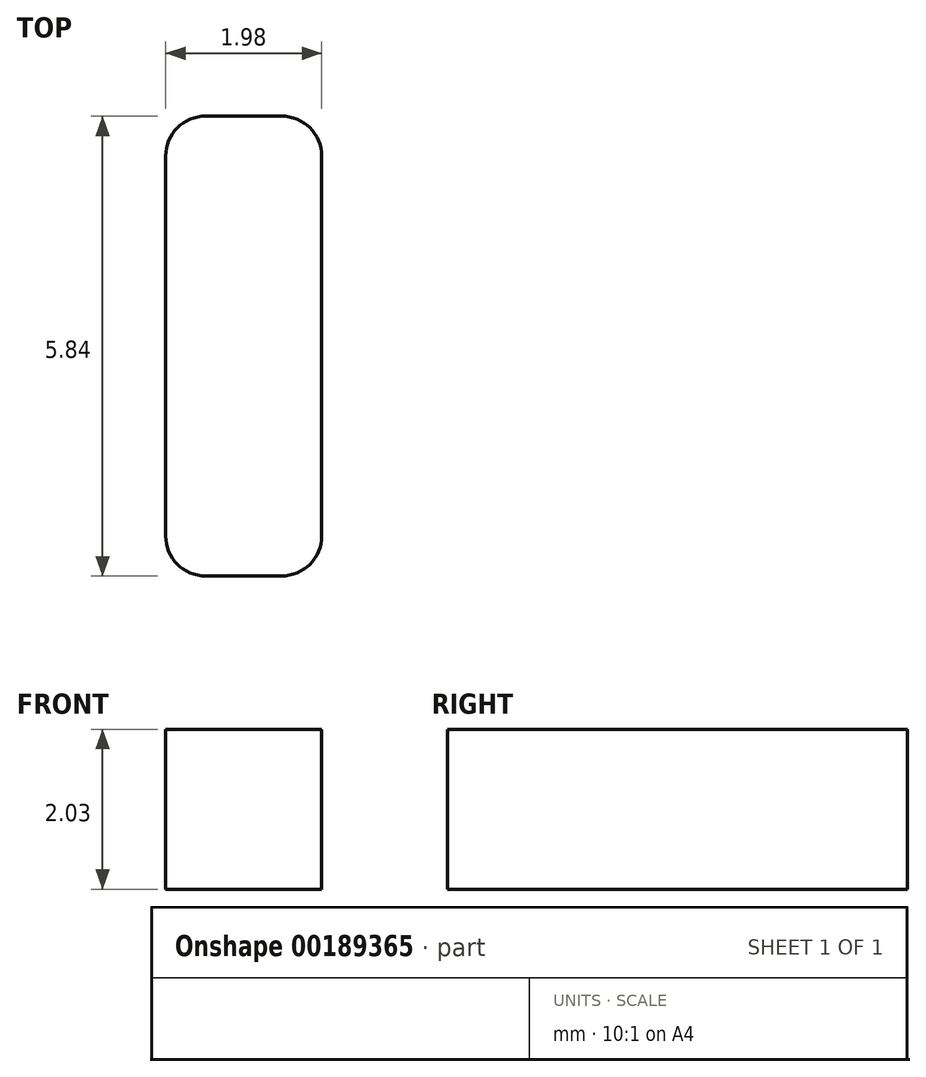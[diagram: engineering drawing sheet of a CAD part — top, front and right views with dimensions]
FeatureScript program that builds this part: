
annotation { "Feature Type Name" : "Feature", "Feature Type Description" : "" }
export const myFeature = defineFeature(function(context is Context, id is Id, definition is map)
    precondition{}
    {
        {
            var Q0;
            Q0=qCreatedBy(makeId("Top.planeOp"),FACE);
            var sketch = newSketch(context, id + "F0", { "sketchPlane" : qUnion([Q0])});
            skLineSegment(sketch, "E0.bottom", {"start": v(0.48, 0) * mm, "end": v(-0.48, 0) * mm});
            skLineSegment(sketch, "E0.top", {"start": v(0.48, 5.84) * mm, "end": v(-0.48, 5.84) * mm});
            skLineSegment(sketch, "E0.left", {"start": v(1, 0.5) * mm, "end": v(1, 5.33) * mm});
            skLineSegment(sketch, "E0.right", {"start": v(-1, 0.5) * mm, "end": v(-1, 5.33) * mm});
            skPoint(sketch, "E1", {"position": v(0, 0) * mm});
            skLineSegment(sketch, "E2", {"start": v(0, -1.94) * mm, "end": v(0, 14.4) * mm, "construction": true});
            skPoint(sketch, "E3.visualSharp", {"position": v(1, 0) * mm});
            skArc(sketch, "E3.filletArc", {"start": v(0.48, 0) * mm, "mid": v(0.84, 0.15) * mm, "end": v(1, 0.5) * mm});
            skPoint(sketch, "E4.visualSharp", {"position": v(-1, 0) * mm});
            skArc(sketch, "E4.filletArc", {"start": v(-1, 0.5) * mm, "mid": v(-0.84, 0.15) * mm, "end": v(-0.48, 0) * mm});
            skPoint(sketch, "E5.visualSharp", {"position": v(-1, 5.84) * mm});
            skArc(sketch, "E5.filletArc", {"start": v(-0.48, 5.84) * mm, "mid": v(-0.84, 5.7) * mm, "end": v(-1, 5.33) * mm});
            skPoint(sketch, "E6.visualSharp", {"position": v(1, 5.84) * mm});
            skArc(sketch, "E6.filletArc", {"start": v(1, 5.33) * mm, "mid": v(0.84, 5.7) * mm, "end": v(0.48, 5.84) * mm});
            skSolve(sketch);
        }
        {
            var Q0;
            Q0=qSketchRegion(id+"F0",true);
            extrude(context, id + "F1", {"entities" : qUnion([Q0]), "depth" : 2.03 * mm});
        }
    });
